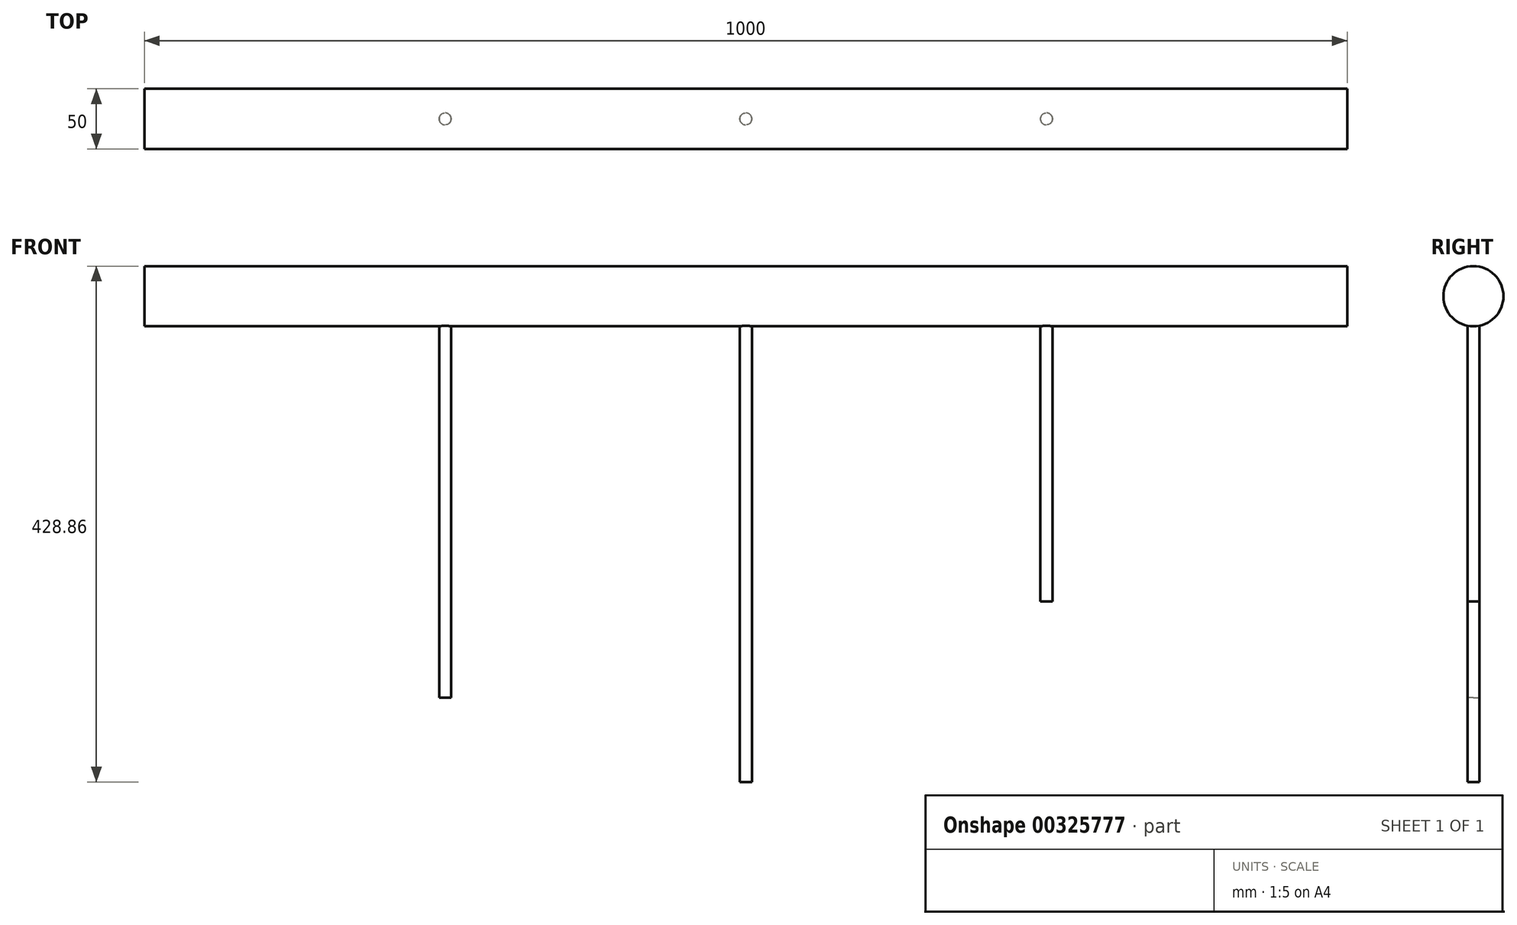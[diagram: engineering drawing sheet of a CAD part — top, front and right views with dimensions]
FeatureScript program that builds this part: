
annotation { "Feature Type Name" : "Feature", "Feature Type Description" : "" }
export const myFeature = defineFeature(function(context is Context, id is Id, definition is map)
    precondition{}
    {
        {
            var Q0;
            Q0=qCreatedBy(makeId("Right.planeOp"),FACE);
            var sketch = newSketch(context, id + "F0", { "sketchPlane" : qUnion([Q0])});
            skCircle(sketch, "E0", {"center": v(0, 53.86) * mm, "radius": 25 * mm});
            skSolve(sketch);
        }
        {
            var Q0;
            Q0 = qSketchRegion(id + "F0", true);
            extrude(context, id + "F1", {"entities" : qUnion([Q0]), "depth" : 1000 * mm});
        }
        {
            var Q0;
            Q0=qCreatedBy(makeId("Top.planeOp"),FACE);
            var sketch = newSketch(context, id + "F2", { "sketchPlane" : qUnion([Q0])});
            skCircle(sketch, "E1", {"center": v(500, 0) * mm, "radius": 5 * mm});
            skCircle(sketch, "E2", {"center": v(250, 0) * mm, "radius": 5 * mm});
            skPoint(sketch, "E3.orphan", {"position": v(0, 0) * mm});
            skCircle(sketch, "E4", {"center": v(750, 0) * mm, "radius": 5 * mm});
            skSolve(sketch);
        }
        {
            var Q0;
            Q0 = qSketchRegion(id + "F2", true);
            extrude(context, id + "F3", {"entities" : qUnion([Q0]), "operationType" : NewBodyOperationType.ADD, "depth" : 50 * mm});
        }
        {
            var Q0;
            Q0=makeQuery(id+"F3.opExtrude","CAP_FACE",FACE,{"disambiguationData":[OSD([sQuery(id+"F2.wireOp",EDGE,"E4")])],"isStart":true});
            var sketch = newSketch(context, id + "F4", { "sketchPlane" : qUnion([Q0])});
            skCircle(sketch, "E5.0", {"center": v(750, 0) * mm, "radius": 5 * mm});
            skSolve(sketch);
        }
        {
            var Q0;
            Q0 = qSketchRegion(id + "F4", true);
            extrude(context, id + "F5", {"entities" : qUnion([Q0]), "operationType" : NewBodyOperationType.ADD, "depth" : 200 * mm});
        }
        {
            var Q0;
            Q0=makeQuery(id+"F3.opExtrude","CAP_FACE",FACE,{"disambiguationData":[OSD([sQuery(id+"F2.wireOp",EDGE,"E1")])],"isStart":true});
            var sketch = newSketch(context, id + "F6", { "sketchPlane" : qUnion([Q0])});
            skCircle(sketch, "E6.0.0", {"center": v(500, 0) * mm, "radius": 5 * mm});
            skSolve(sketch);
        }
        {
            var Q0;
            Q0 = qSketchRegion(id + "F6", true);
            extrude(context, id + "F7", {"entities" : qUnion([Q0]), "operationType" : NewBodyOperationType.ADD, "depth" : 350 * mm});
        }
        {
            var Q0;
            Q0=makeQuery(id+"F3.opExtrude","CAP_FACE",FACE,{"disambiguationData":[OSD([sQuery(id+"F2.wireOp",EDGE,"E2")])],"isStart":true});
            var sketch = newSketch(context, id + "F8", { "sketchPlane" : qUnion([Q0])});
            skCircle(sketch, "E7.0.0", {"center": v(250, 0) * mm, "radius": 5 * mm});
            skSolve(sketch);
        }
        {
            var Q0;
            Q0 = qSketchRegion(id + "F8", true);
            extrude(context, id + "F9", {"entities" : qUnion([Q0]), "operationType" : NewBodyOperationType.ADD, "depth" : 280 * mm});
        }
    });
